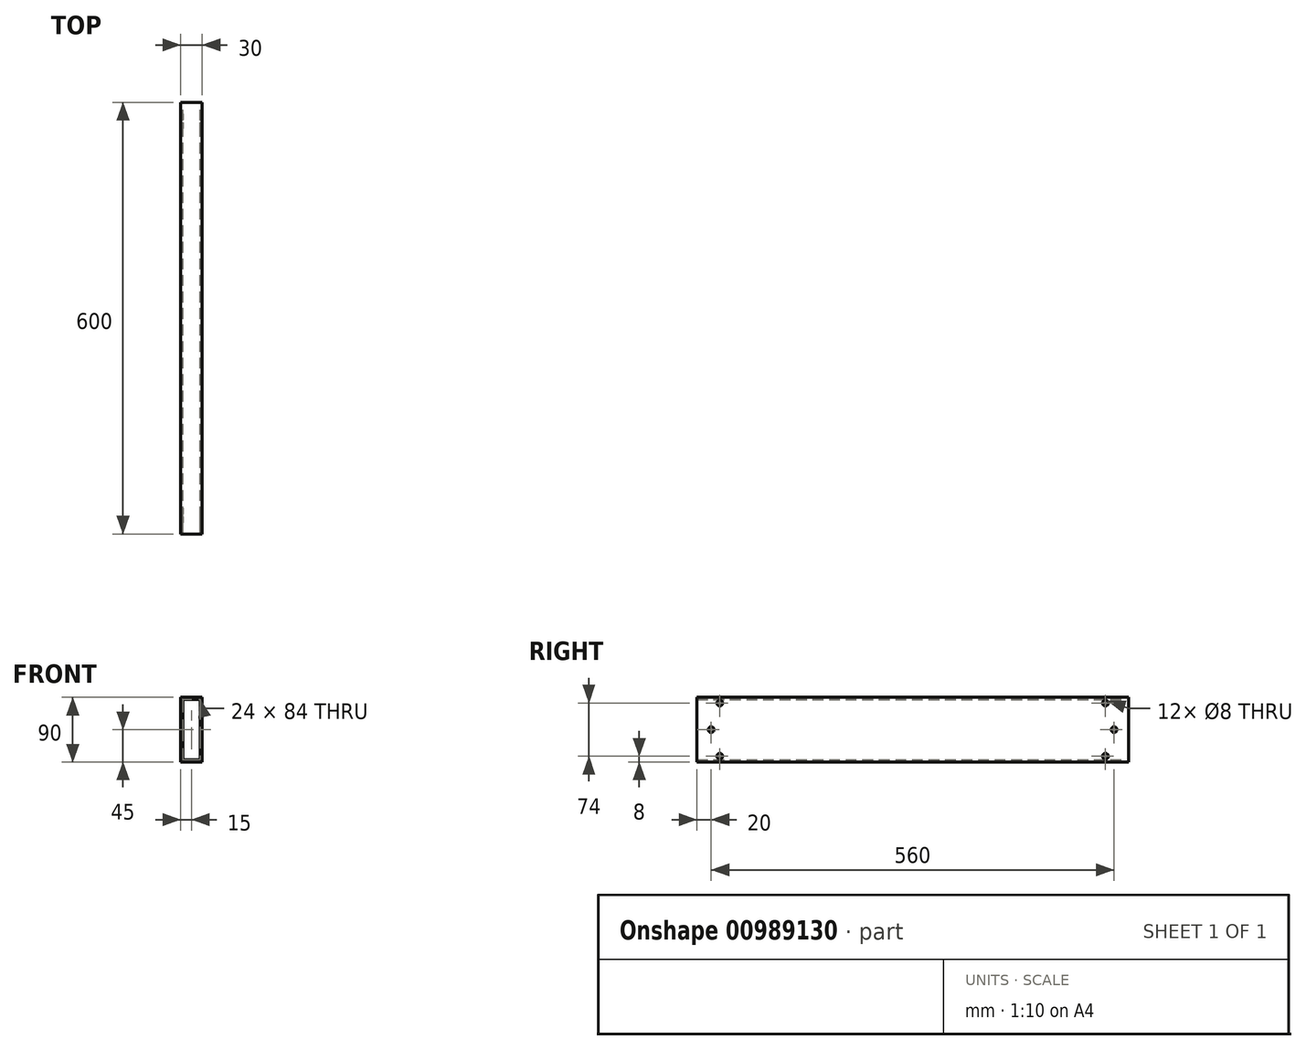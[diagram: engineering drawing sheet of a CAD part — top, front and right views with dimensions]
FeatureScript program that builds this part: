
annotation { "Feature Type Name" : "Feature", "Feature Type Description" : "" }
export const myFeature = defineFeature(function(context is Context, id is Id, definition is map)
    precondition{}
    {
        {
            var Q0;
            Q0=qCreatedBy(makeId("Front.planeOp"),FACE);
            var sketch = newSketch(context, id + "F0", { "sketchPlane" : qUnion([Q0])});
            skLineSegment(sketch, "E0.bottom", {"start": v(15, 45) * mm, "end": v(-15, 45) * mm});
            skLineSegment(sketch, "E0.top", {"start": v(15, -45) * mm, "end": v(-15, -45) * mm});
            skLineSegment(sketch, "E0.left", {"start": v(15, 45) * mm, "end": v(15, -45) * mm});
            skLineSegment(sketch, "E0.right", {"start": v(-15, 45) * mm, "end": v(-15, -45) * mm});
            skPoint(sketch, "E0.middle", {"position": v(0, 0) * mm});
            skSolve(sketch);
        }
        {
            var Q0;
            Q0=qSketchRegion(id+"F0",true);
            extrude(context, id + "F1", {"entities" : qUnion([Q0]), "endBound" : BoundingType.SYMMETRIC, "depth" : 600 * mm, "offsetDistance" : 25.4 * mm});
        }
        {
            var Q0;
            Q0=makeQuery(id+"F1.opExtrude","CAP_FACE",FACE,{"disambiguationData":[OSD([sQuery(id+"F0.wireOp",EDGE,"E0.bottom"),sQuery(id+"F0.wireOp",EDGE,"E0.top"),sQuery(id+"F0.wireOp",EDGE,"E0.left"),sQuery(id+"F0.wireOp",EDGE,"E0.right")])],"isStart":false});
            var Q1;
            Q1=makeQuery(id+"F1.opExtrude","CAP_FACE",FACE,{"disambiguationData":[OSD([sQuery(id+"F0.wireOp",EDGE,"E0.bottom"),sQuery(id+"F0.wireOp",EDGE,"E0.top"),sQuery(id+"F0.wireOp",EDGE,"E0.left"),sQuery(id+"F0.wireOp",EDGE,"E0.right")])],"isStart":true});
            shell(context, id + "F2", {"entities" : qUnion([Q0, Q1]), "thickness" : 3 * mm});
        }
        {
            var Q0;
            Q0=makeQuery(id+"F1.opExtrude","SWEPT_FACE",FACE,{"disambiguationData":[OSD([sQuery(id+"F0.wireOp",EDGE,"E0.left")])]});
            var sketch = newSketch(context, id + "F3", { "sketchPlane" : qUnion([Q0])});
            skLineSegment(sketch, "E1", {"start": v(14, 0) * mm, "end": v(-300, 0) * mm, "construction": true});
            skCircle(sketch, "E2", {"center": v(-268, 37) * mm, "radius": 4 * mm});
            skCircle(sketch, "E3", {"center": v(-280, 0) * mm, "radius": 4 * mm});
            skCircle(sketch, "E4", {"center": v(-268, -37) * mm, "radius": 4 * mm});
            skSolve(sketch);
        }
        {
            var Q0;
            Q0 = qSketchRegion(id + "F3", true);
            extrude(context, id + "F4", {"entities" : qUnion([Q0]), "operationType" : NewBodyOperationType.REMOVE, "endBound" : BoundingType.THROUGH_ALL, "oppositeDirection" : true, "depth" : 25 * mm, "offsetDistance" : 25 * mm});
        }
        {
            var Q0;
            Q0=makeQuery(id+"F1.opExtrude","CAP_FACE",FACE,{"disambiguationData":[OSD([sQuery(id+"F0.wireOp",EDGE,"E0.bottom"),sQuery(id+"F0.wireOp",EDGE,"E0.top"),sQuery(id+"F0.wireOp",EDGE,"E0.left"),sQuery(id+"F0.wireOp",EDGE,"E0.right")])],"isStart":false});
            cPlane(context, id + "F5", {"entities" : qUnion([Q0]), "cplaneType" : CPlaneType.OFFSET, "offset" : 50 * mm, "oppositeDirection" : true, "width" : 150 * mm, "height" : 150 * mm});
        }
        {
            var Q0;
            Q0=makeQuery(id+"F1.opExtrude","CAP_FACE",FACE,{"disambiguationData":[OSD([sQuery(id+"F0.wireOp",EDGE,"E0.bottom"),sQuery(id+"F0.wireOp",EDGE,"E0.top"),sQuery(id+"F0.wireOp",EDGE,"E0.left"),sQuery(id+"F0.wireOp",EDGE,"E0.right")])],"isStart":true});
            cPlane(context, id + "F6", {"entities" : qUnion([Q0]), "cplaneType" : CPlaneType.OFFSET, "offset" : 50 * mm, "oppositeDirection" : true, "width" : 150 * mm, "height" : 150 * mm});
        }
        {
            var Q0;
            Q0=makeQuery(id+"F1.opExtrude","SWEPT_FACE",FACE,{"disambiguationData":[OSD([sQuery(id+"F0.wireOp",EDGE,"E0.left")])]});
            var sketch = newSketch(context, id + "F7", { "sketchPlane" : qUnion([Q0])});
            skLineSegment(sketch, "E5", {"start": v(300, 0) * mm, "end": v(260, 0) * mm, "construction": true});
            skCircle(sketch, "E6", {"center": v(268, 37) * mm, "radius": 4 * mm});
            skCircle(sketch, "E7", {"center": v(280, 0) * mm, "radius": 4 * mm});
            skCircle(sketch, "E8", {"center": v(268, -37) * mm, "radius": 4 * mm});
            skSolve(sketch);
        }
        {
            var Q0;
            Q0 = qSketchRegion(id + "F7", true);
            extrude(context, id + "F8", {"entities" : qUnion([Q0]), "operationType" : NewBodyOperationType.REMOVE, "endBound" : BoundingType.THROUGH_ALL, "oppositeDirection" : true, "depth" : 25 * mm, "offsetDistance" : 25 * mm});
        }
    });
